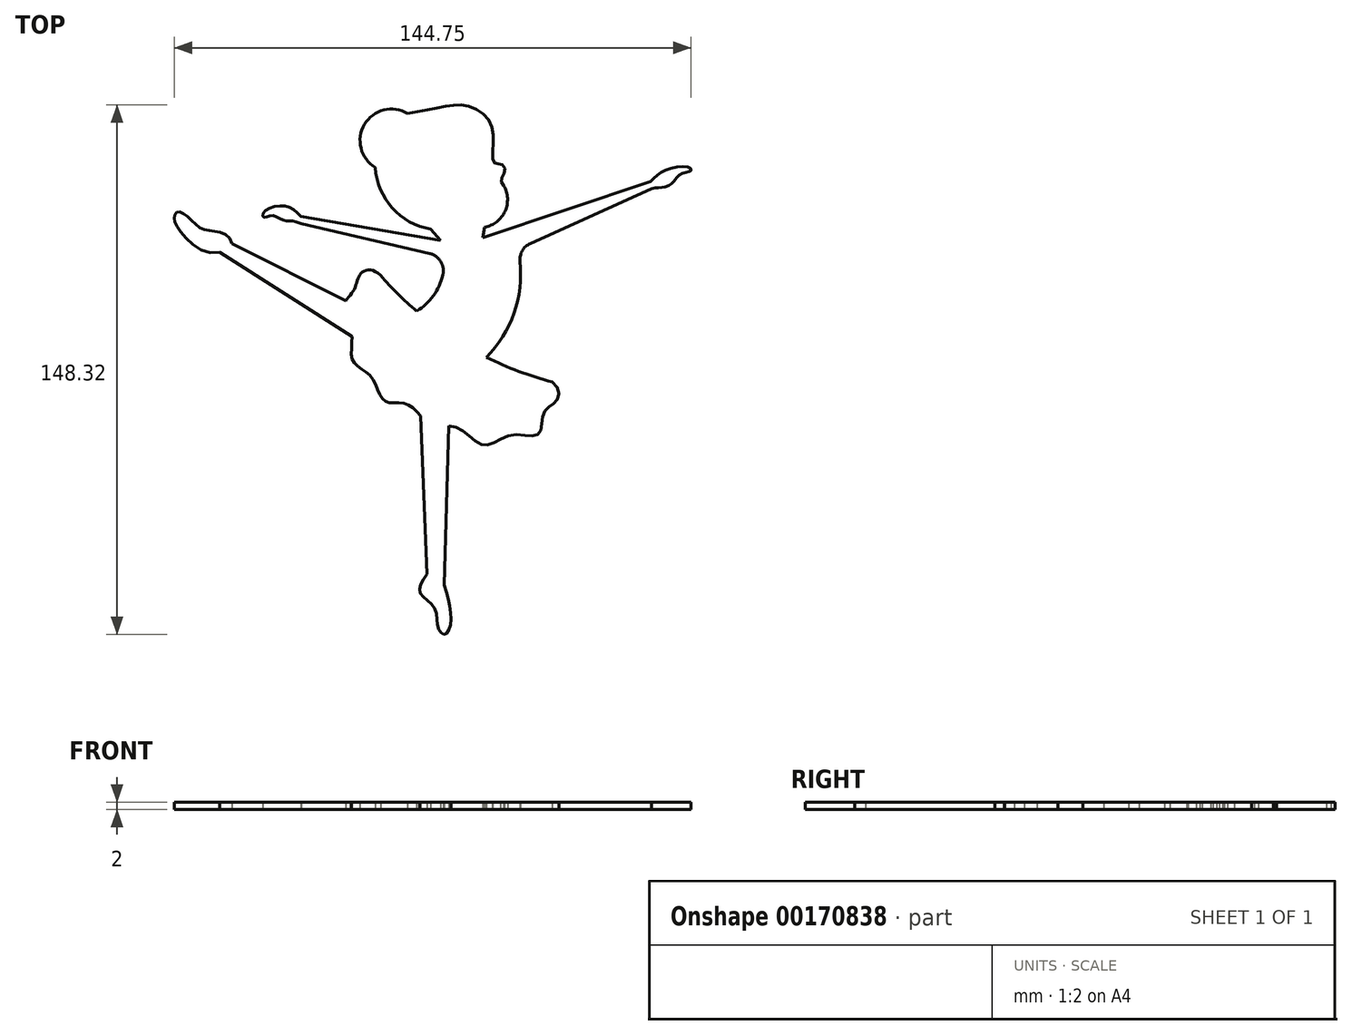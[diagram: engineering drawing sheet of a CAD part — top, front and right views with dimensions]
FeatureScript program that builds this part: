
annotation { "Feature Type Name" : "Feature", "Feature Type Description" : "" }
export const myFeature = defineFeature(function(context is Context, id is Id, definition is map)
    precondition{}
    {
        {
            var Q0;
            Q0=qCreatedBy(makeId("Top.planeOp"),FACE);
            var sketch = newSketch(context, id + "F0", { "sketchPlane" : qUnion([Q0])});
            skLineSegment(sketch, "E0.bottom", {"start": v(71.52, 69.3) * mm, "end": v(-73.48, 69.3) * mm, "construction": true});
            skLineSegment(sketch, "E0.top", {"start": v(71.52, -80.7) * mm, "end": v(-73.48, -80.7) * mm, "construction": true});
            skLineSegment(sketch, "E0.left", {"start": v(71.52, 69.3) * mm, "end": v(71.52, -80.7) * mm, "construction": true});
            skLineSegment(sketch, "E0.right", {"start": v(-73.48, 69.3) * mm, "end": v(-73.48, -80.7) * mm, "construction": true});
            skPoint(sketch, "E0.middle", {"position": v(-0.98, -5.7) * mm});
            skSolve(sketch);
        }
        {
            var Q0;
            Q0=qCreatedBy(makeId("Top.planeOp"),FACE);
            var sketch = newSketch(context, id + "F1", { "sketchPlane" : qUnion([Q0])});
            skFitSpline(sketch, "E1", {"points": [v(-60.08, 28.51) * mm, v(-71.57, 34.94) * mm, v(-72.8, 38.28) * mm, v(-71.89, 39.73) * mm, v(-69.35, 38.65) * mm, v(-65.4, 35.19) * mm, v(-60.7, 34.2) * mm, v(-56.61, 30.86) * mm], "startDerivative": vector(-64.05, -17.21) * mm, "endDerivative": vector(6.7, -44.27) * mm});
            skLineSegment(sketch, "E2", {"start": v(-56.61, 30.86) * mm, "end": v(-24.74, 14.87) * mm});
            skLineSegment(sketch, "E3", {"start": v(-60.08, 28.51) * mm, "end": v(-22.97, 4.86) * mm});
            skArc(sketch, "E4", {"start": v(-15.06, 21.97) * mm, "mid": v(6.75, 3.41) * mm, "end": v(33.05, -7.9) * mm});
            skFitSpline(sketch, "E5", {"points": [v(-15.06, 21.97) * mm, v(-20.5, 22.58) * mm, v(-22.47, 17.96) * mm, v(-25.37, 13.32) * mm, v(-23.13, 7.4) * mm, v(-22.8, -1.84) * mm, v(-17.68, -6.44) * mm, v(-13.9, -13.23) * mm, v(-7.73, -14.11) * mm, v(-1.25, -19.33) * mm, v(6.65, -20.78) * mm, v(13.8, -25.55) * mm, v(21.58, -22.77) * mm, v(29.26, -22.4) * mm, v(30.75, -16.38) * mm, v(34.27, -13.14) * mm, v(33.05, -7.9) * mm], "startDerivative": vector(-108.73, 113.06) * mm, "endDerivative": vector(-113.44, 75.6) * mm});
            skFitSpline(sketch, "E6", {"points": [v(2.8, -64.81) * mm, v(4.66, -74.61) * mm, v(3.03, -78.58) * mm, v(1.16, -76.95) * mm, v(0, -71.1) * mm, v(-3.97, -66.91) * mm, v(-2.1, -61.78) * mm], "startDerivative": vector(13.36, -45.37) * mm, "endDerivative": vector(23.76, 31.88) * mm});
            skLineSegment(sketch, "E7", {"start": v(-2.1, -61.78) * mm, "end": v(-3.79, -17.34) * mm});
            skLineSegment(sketch, "E8", {"start": v(2.8, -64.81) * mm, "end": v(4.05, -20.15) * mm});
            skFitSpline(sketch, "E9", {"points": [v(-37.35, 38.48) * mm, v(-42.32, 41.48) * mm, v(-47.9, 39.42) * mm, v(-47.69, 38.24) * mm, v(-45.41, 38.76) * mm, v(-42.15, 37.37) * mm, v(-39.53, 37.23) * mm, v(-37.17, 36.48) * mm], "startDerivative": vector(-21.92, 25.22) * mm, "endDerivative": vector(18.41, -2.51) * mm});
            skLineSegment(sketch, "E10", {"start": v(-37.35, 38.48) * mm, "end": v(1.74, 31.82) * mm});
            skLineSegment(sketch, "E11", {"start": v(-37.17, 36.48) * mm, "end": v(-1.32, 28.1) * mm});
            skArc(sketch, "E12", {"start": v(-4.94, 11.95) * mm, "mid": v(-0.28, 16.27) * mm, "end": v(2.4, 22.05) * mm});
            skLineSegment(sketch, "E13", {"start": v(13.6, 32.47) * mm, "end": v(60.59, 48.27) * mm});
            skLineSegment(sketch, "E14", {"start": v(26.9, 30.93) * mm, "end": v(60.86, 46.3) * mm});
            skArc(sketch, "E15", {"start": v(14.62, -0.98) * mm, "mid": v(22.3, 11.4) * mm, "end": v(24, 25.86) * mm});
            skLineSegment(sketch, "E16", {"start": v(1.74, 31.82) * mm, "end": v(-1, 34.93) * mm});
            skLineSegment(sketch, "E17", {"start": v(13.6, 32.47) * mm, "end": v(13.6, 32.47) * mm});
            skLineSegment(sketch, "E18", {"start": v(13.6, 32.47) * mm, "end": v(14.13, 35.49) * mm});
            skArc(sketch, "E19", {"start": v(-16.5, 52.2) * mm, "mid": v(-11.77, 40.86) * mm, "end": v(-1, 34.93) * mm});
            skArc(sketch, "E20", {"start": v(-7.47, 67.31) * mm, "mid": v(-19.54, 64.27) * mm, "end": v(-16.5, 52.2) * mm});
            skArc(sketch, "E21", {"start": v(14.13, 35.49) * mm, "mid": v(19.8, 39.91) * mm, "end": v(19.44, 47.1) * mm});
            skFitSpline(sketch, "E22", {"points": [v(-7.47, 67.31) * mm, v(2.93, 69.27) * mm, v(9.65, 69.36) * mm, v(15.54, 65.04) * mm, v(16.47, 58.09) * mm, v(16.87, 53.4) * mm, v(18.6, 53.18) * mm, v(19.82, 51.51) * mm, v(18.73, 48.83) * mm, v(19.44, 47.1) * mm], "startDerivative": vector(63.99, 12.21) * mm, "endDerivative": vector(16.59, -26) * mm});
            skFitSpline(sketch, "E23", {"points": [v(60.59, 48.27) * mm, v(65.03, 51.61) * mm, v(71.67, 51.98) * mm, v(71.75, 51.17) * mm, v(69.03, 50.43) * mm, v(66.6, 47.79) * mm, v(63.74, 46.6) * mm, v(60.86, 46.3) * mm], "startDerivative": vector(21.57, 20.42) * mm, "endDerivative": vector(-21.74, -7.17) * mm});
            skPoint(sketch, "E24.visualSharp", {"position": v(23.45, 29.36) * mm});
            skArc(sketch, "E24.filletArc", {"start": v(26.9, 30.93) * mm, "mid": v(24.64, 28.86) * mm, "end": v(24, 25.86) * mm});
            skPoint(sketch, "E25.visualSharp", {"position": v(2.83, 27.13) * mm});
            skArc(sketch, "E25.filletArc", {"start": v(2.4, 22.05) * mm, "mid": v(1.8, 25.85) * mm, "end": v(-1.32, 28.1) * mm});
            skSolve(sketch);
        }
        {
            var Q0;
            Q0=makeQuery(id+"F1.imprint","IMPRINT",FACE,{"disambiguationData":[TD([[makeQuery(id+"F1.imprint","IMPRINT",EDGE,{"derivedFrom":sQuery(id+"F1.wireOp",EDGE,"E9")}),1.0]])]});
            var Q1;
            {var subQ0=sQuery(id+"F1.wireOp",EDGE,"E5");var subQ1=sQuery(id+"F1.wireOp",EDGE,"E4");var subQ5=makeQuery(id+"F1.imprint","INTERSECT",VERTEX,{"disambiguationData":[OD(0.0)],"derivedFrom":[subQ1,subQ0]});Q1=makeQuery(id+"F1.imprint","IMPRINT",FACE,{"disambiguationData":[TD([[makeQuery(id+"F1.imprint","IMPRINT",EDGE,{"disambiguationData":[TD([[subQ5,-1.0]])],"derivedFrom":subQ1}),-1.0]])]});}
            var Q2;
            Q2=makeQuery(id+"F1.imprint","IMPRINT",FACE,{"disambiguationData":[TD([[makeQuery(id+"F1.imprint","IMPRINT",EDGE,{"derivedFrom":sQuery(id+"F1.wireOp",EDGE,"E6")}),-1.0]])]});
            var Q3;
            Q3=makeQuery(id+"F1.imprint","IMPRINT",FACE,{"disambiguationData":[TD([[makeQuery(id+"F1.imprint","IMPRINT",EDGE,{"derivedFrom":sQuery(id+"F1.wireOp",EDGE,"E1")}),-1.0]])]});
            extrude(context, id + "F2", {"entities" : qUnion([Q0, Q1, Q2, Q3]), "depth" : 2 * mm});
        }
    });
